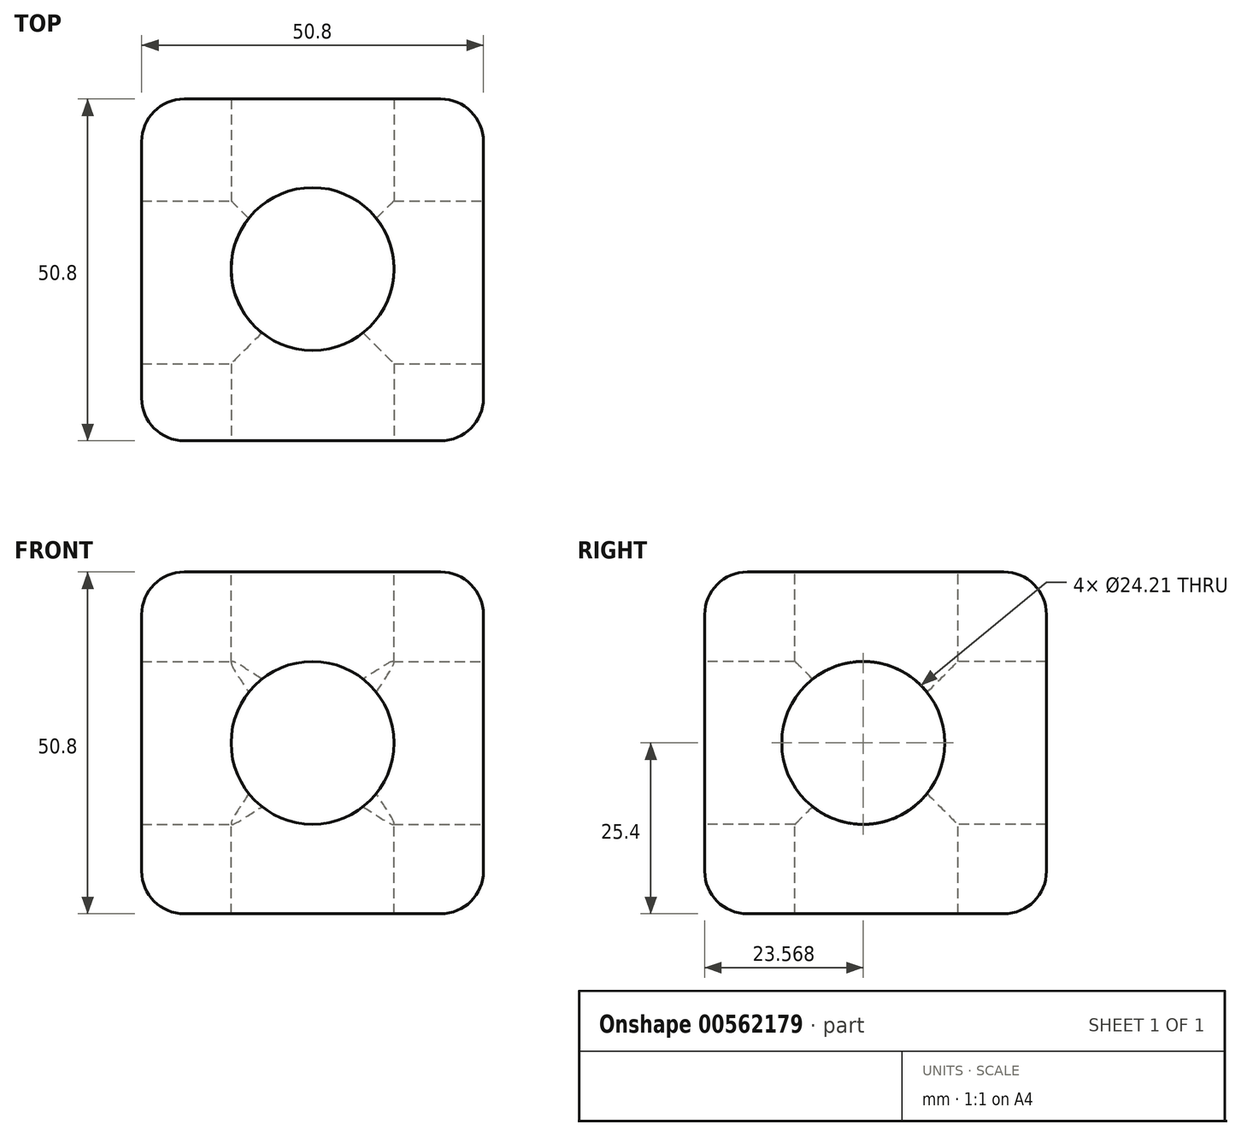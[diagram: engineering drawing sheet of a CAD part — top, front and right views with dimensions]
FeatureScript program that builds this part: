
annotation { "Feature Type Name" : "Feature", "Feature Type Description" : "" }
export const myFeature = defineFeature(function(context is Context, id is Id, definition is map)
    precondition{}
    {
        {
            var Q0;
            Q0=qCreatedBy(makeId("Front.planeOp"),FACE);
            var sketch = newSketch(context, id + "F0", { "sketchPlane" : qUnion([Q0])});
            skLineSegment(sketch, "E0.bottom", {"start": v(25.4, 25.4) * mm, "end": v(-25.4, 25.4) * mm});
            skLineSegment(sketch, "E0.top", {"start": v(25.4, -25.4) * mm, "end": v(-25.4, -25.4) * mm});
            skLineSegment(sketch, "E0.left", {"start": v(25.4, 25.4) * mm, "end": v(25.4, -25.4) * mm});
            skLineSegment(sketch, "E0.right", {"start": v(-25.4, 25.4) * mm, "end": v(-25.4, -25.4) * mm});
            skPoint(sketch, "E0.middle", {"position": v(0, 0) * mm});
            skSolve(sketch);
        }
        {
            var Q0;
            Q0=makeQuery(id+"F0.imprint","IMPRINT",FACE,{"disambiguationData":[TD([[makeQuery(id+"F0.imprint","IMPRINT",EDGE,{"derivedFrom":sQuery(id+"F0.wireOp",EDGE,"E0.bottom")}),1.0]])]});
            extrude(context, id + "F1", {"entities" : qUnion([Q0]), "depth" : 50.8 * mm, "offsetDistance" : 25.4 * mm});
        }
        {
            var Q0;
            Q0=makeQuery(id+"F1.opExtrude","CAP_FACE",FACE,{"disambiguationData":[OSD([sQuery(id+"F0.wireOp",EDGE,"E0.bottom"),sQuery(id+"F0.wireOp",EDGE,"E0.top"),sQuery(id+"F0.wireOp",EDGE,"E0.left"),sQuery(id+"F0.wireOp",EDGE,"E0.right")])],"isStart":false});
            var sketch = newSketch(context, id + "F2", { "sketchPlane" : qUnion([Q0])});
            skPoint(sketch, "E1", {"position": v(0, 0) * mm});
            skSolve(sketch);
        }
        {
            var Q0;
            Q0=sQuery(id+"F2.wireOp",VERTEX,"E1");
            var Q1;
            Q1=makeQuery(id+"F1.opExtrude","SWEPT_BODY",BODY,{"disambiguationData":[OSD([sQuery(id+"F0.wireOp",EDGE,"E0.bottom"),sQuery(id+"F0.wireOp",EDGE,"E0.top"),sQuery(id+"F0.wireOp",EDGE,"E0.left"),sQuery(id+"F0.wireOp",EDGE,"E0.right")])]});
            hole(context, id + "F3", {"style" : HoleStyle.SIMPLE, "endStyle" : HoleEndStyle.THROUGH, "standardTappedOrClearance" : lookupTablePath({ "standard" : "ANSI", "engagement" : "75%", "pitch" : "20 tpi", "size" : "1", "type" : "Tapped" }), "standardBlindInLast" : lookupTablePath({ "standard" : "ANSI", "engagement" : "75%", "pitch" : "20 tpi", "size" : "1", "type" : "Tapped" }), "holeDiameter" : 24.2 * mm, "showTappedDepth" : true, "isTappedThrough" : true, "tappedDepth" : 12.7 * mm, "tapClearance" : 3, "locations" : qUnion([Q0]), "scope" : qUnion([Q1]), "majorDiameter" : 25.4 * mm});
        }
        {
            var Q0;
            Q0=makeQuery(id+"F1.opExtrude","SWEPT_FACE",FACE,{"disambiguationData":[OSD([sQuery(id+"F0.wireOp",EDGE,"E0.bottom")])]});
            var sketch = newSketch(context, id + "F4", { "sketchPlane" : qUnion([Q0])});
            skPoint(sketch, "E2", {"position": v(0, -25.27) * mm});
            skSolve(sketch);
        }
        {
            var Q0;
            Q0=sQuery(id+"F4.wireOp",VERTEX,"E2");
            var Q1;
            Q1=makeQuery(id+"F1.opExtrude","SWEPT_BODY",BODY,{"disambiguationData":[OSD([sQuery(id+"F0.wireOp",EDGE,"E0.bottom"),sQuery(id+"F0.wireOp",EDGE,"E0.top"),sQuery(id+"F0.wireOp",EDGE,"E0.left"),sQuery(id+"F0.wireOp",EDGE,"E0.right")])]});
            hole(context, id + "F5", {"style" : HoleStyle.SIMPLE, "endStyle" : HoleEndStyle.THROUGH, "standardTappedOrClearance" : lookupTablePath({ "standard" : "ANSI", "engagement" : "75%", "pitch" : "20 tpi", "size" : "1", "type" : "Tapped" }), "standardBlindInLast" : lookupTablePath({ "standard" : "ANSI", "engagement" : "75%", "pitch" : "20 tpi", "size" : "1", "type" : "Tapped" }), "holeDiameter" : 24.2 * mm, "showTappedDepth" : true, "isTappedThrough" : true, "tappedDepth" : 12.7 * mm, "tapClearance" : 3, "locations" : qUnion([Q0]), "scope" : qUnion([Q1]), "majorDiameter" : 25.4 * mm});
        }
        {
            var Q0;
            Q0=makeQuery(id+"F1.opExtrude","SWEPT_FACE",FACE,{"disambiguationData":[OSD([sQuery(id+"F0.wireOp",EDGE,"E0.left")])]});
            var sketch = newSketch(context, id + "F6", { "sketchPlane" : qUnion([Q0])});
            skPoint(sketch, "E3", {"position": v(-27.23, 0) * mm});
            skSolve(sketch);
        }
        {
            var Q0;
            Q0=sQuery(id+"F6.wireOp",VERTEX,"E3");
            var Q1;
            Q1=makeQuery(id+"F1.opExtrude","SWEPT_BODY",BODY,{"disambiguationData":[OSD([sQuery(id+"F0.wireOp",EDGE,"E0.bottom"),sQuery(id+"F0.wireOp",EDGE,"E0.top"),sQuery(id+"F0.wireOp",EDGE,"E0.left"),sQuery(id+"F0.wireOp",EDGE,"E0.right")])]});
            hole(context, id + "F7", {"style" : HoleStyle.SIMPLE, "endStyle" : HoleEndStyle.THROUGH, "standardTappedOrClearance" : lookupTablePath({ "standard" : "ANSI", "engagement" : "75%", "pitch" : "20 tpi", "size" : "1", "type" : "Tapped" }), "standardBlindInLast" : lookupTablePath({ "standard" : "ANSI", "engagement" : "75%", "pitch" : "20 tpi", "size" : "1", "type" : "Tapped" }), "holeDiameter" : 24.2 * mm, "showTappedDepth" : true, "isTappedThrough" : true, "tappedDepth" : 12.7 * mm, "tapClearance" : 3, "locations" : qUnion([Q0]), "scope" : qUnion([Q1]), "majorDiameter" : 25.4 * mm});
        }
        {
            var Q0;
            Q0=makeQuery(id+"F1.opExtrude","CAP_EDGE",EDGE,{"disambiguationData":[OSD([sQuery(id+"F0.wireOp",EDGE,"E0.bottom")])],"isStart":false});
            var Q1;
            Q1=makeQuery(id+"F1.opExtrude","SWEPT_EDGE",EDGE,{"disambiguationData":[OSD([sQuery(id+"F0.wireOp",EDGE,"E0.bottom"),sQuery(id+"F0.wireOp",EDGE,"E0.left")])]});
            var Q2;
            Q2=makeQuery(id+"F1.opExtrude","CAP_EDGE",EDGE,{"disambiguationData":[OSD([sQuery(id+"F0.wireOp",EDGE,"E0.left")])],"isStart":false});
            var Q3;
            Q3=makeQuery(id+"F1.opExtrude","SWEPT_EDGE",EDGE,{"disambiguationData":[OSD([sQuery(id+"F0.wireOp",EDGE,"E0.top"),sQuery(id+"F0.wireOp",EDGE,"E0.left")])]});
            var Q4;
            Q4=makeQuery(id+"F1.opExtrude","CAP_EDGE",EDGE,{"disambiguationData":[OSD([sQuery(id+"F0.wireOp",EDGE,"E0.left")])],"isStart":true});
            var Q5;
            Q5=makeQuery(id+"F1.opExtrude","CAP_EDGE",EDGE,{"disambiguationData":[OSD([sQuery(id+"F0.wireOp",EDGE,"E0.bottom")])],"isStart":true});
            var Q6;
            Q6=makeQuery(id+"F1.opExtrude","SWEPT_EDGE",EDGE,{"disambiguationData":[OSD([sQuery(id+"F0.wireOp",EDGE,"E0.bottom"),sQuery(id+"F0.wireOp",EDGE,"E0.right")])]});
            var Q7;
            Q7=makeQuery(id+"F1.opExtrude","CAP_EDGE",EDGE,{"disambiguationData":[OSD([sQuery(id+"F0.wireOp",EDGE,"E0.right")])],"isStart":false});
            var Q8;
            Q8=makeQuery(id+"F1.opExtrude","CAP_EDGE",EDGE,{"disambiguationData":[OSD([sQuery(id+"F0.wireOp",EDGE,"E0.top")])],"isStart":false});
            var Q9;
            Q9=makeQuery(id+"F1.opExtrude","CAP_EDGE",EDGE,{"disambiguationData":[OSD([sQuery(id+"F0.wireOp",EDGE,"E0.top")])],"isStart":true});
            var Q10;
            Q10=makeQuery(id+"F1.opExtrude","SWEPT_EDGE",EDGE,{"disambiguationData":[OSD([sQuery(id+"F0.wireOp",EDGE,"E0.top"),sQuery(id+"F0.wireOp",EDGE,"E0.right")])]});
            var Q11;
            Q11=makeQuery(id+"F1.opExtrude","CAP_EDGE",EDGE,{"disambiguationData":[OSD([sQuery(id+"F0.wireOp",EDGE,"E0.right")])],"isStart":true});
            var Q12;
            Q12=makeQuery(id+"F5.hole-0.boolean.opBoolean","COPY",EDGE,{"derivedFrom":makeQuery(id+"F5.hole-0.opRevolve","SWEPT_EDGE",EDGE,{"disambiguationData":[OSD([sQuery(id+"F5.hole-0.sketch.wireOp",EDGE,"core_line_2"),sQuery(id+"F5.hole-0.sketch.wireOp",EDGE,"core_line_3")])]})});
            var Q13;
            Q13=makeQuery(id+"F3.hole-0.boolean.opBoolean","COPY",EDGE,{"derivedFrom":makeQuery(id+"F3.hole-0.opRevolve","SWEPT_EDGE",EDGE,{"disambiguationData":[OSD([sQuery(id+"F3.hole-0.sketch.wireOp",EDGE,"core_line_2"),sQuery(id+"F3.hole-0.sketch.wireOp",EDGE,"core_line_3")])]})});
            var Q14;
            Q14=makeQuery(id+"F7.hole-0.boolean.opBoolean","COPY",EDGE,{"derivedFrom":makeQuery(id+"F7.hole-0.opRevolve","SWEPT_EDGE",EDGE,{"disambiguationData":[OSD([sQuery(id+"F7.hole-0.sketch.wireOp",EDGE,"core_line_2"),sQuery(id+"F7.hole-0.sketch.wireOp",EDGE,"core_line_3")])]})});
            var Q15;
            Q15=makeQuery(id+"F5.hole-0.boolean.opBoolean","INTERSECT",EDGE,{"derivedFrom":[makeQuery(id+"F1.opExtrude","SWEPT_FACE",FACE,{"disambiguationData":[OSD([sQuery(id+"F0.wireOp",EDGE,"E0.top")])]}),makeQuery(id+"F5.hole-0.opRevolve","SWEPT_FACE",FACE,{"disambiguationData":[OSD([sQuery(id+"F5.hole-0.sketch.wireOp",EDGE,"core_line_2")])]})]});
            var Q16;
            Q16=makeQuery(id+"F3.hole-0.boolean.opBoolean","INTERSECT",EDGE,{"derivedFrom":[makeQuery(id+"F1.opExtrude","CAP_FACE",FACE,{"disambiguationData":[OSD([sQuery(id+"F0.wireOp",EDGE,"E0.bottom"),sQuery(id+"F0.wireOp",EDGE,"E0.top"),sQuery(id+"F0.wireOp",EDGE,"E0.left"),sQuery(id+"F0.wireOp",EDGE,"E0.right")])],"isStart":true}),makeQuery(id+"F3.hole-0.opRevolve","SWEPT_FACE",FACE,{"disambiguationData":[OSD([sQuery(id+"F3.hole-0.sketch.wireOp",EDGE,"core_line_2")])]})]});
            var Q17;
            Q17=makeQuery(id+"F7.hole-0.boolean.opBoolean","INTERSECT",EDGE,{"derivedFrom":[makeQuery(id+"F1.opExtrude","SWEPT_FACE",FACE,{"disambiguationData":[OSD([sQuery(id+"F0.wireOp",EDGE,"E0.right")])]}),makeQuery(id+"F7.hole-0.opRevolve","SWEPT_FACE",FACE,{"disambiguationData":[OSD([sQuery(id+"F7.hole-0.sketch.wireOp",EDGE,"core_line_2")])]})]});
            fillet(context, id + "F8", {"entities" : qUnion([Q0, Q1, Q2, Q3, Q4, Q5, Q6, Q7, Q8, Q9, Q10, Q11, Q12, Q13, Q14, Q15, Q16, Q17]), "radius" : 6.35 * mm, "tangentPropagation" : true, "allowEdgeOverflow" : false});
        }
    });
